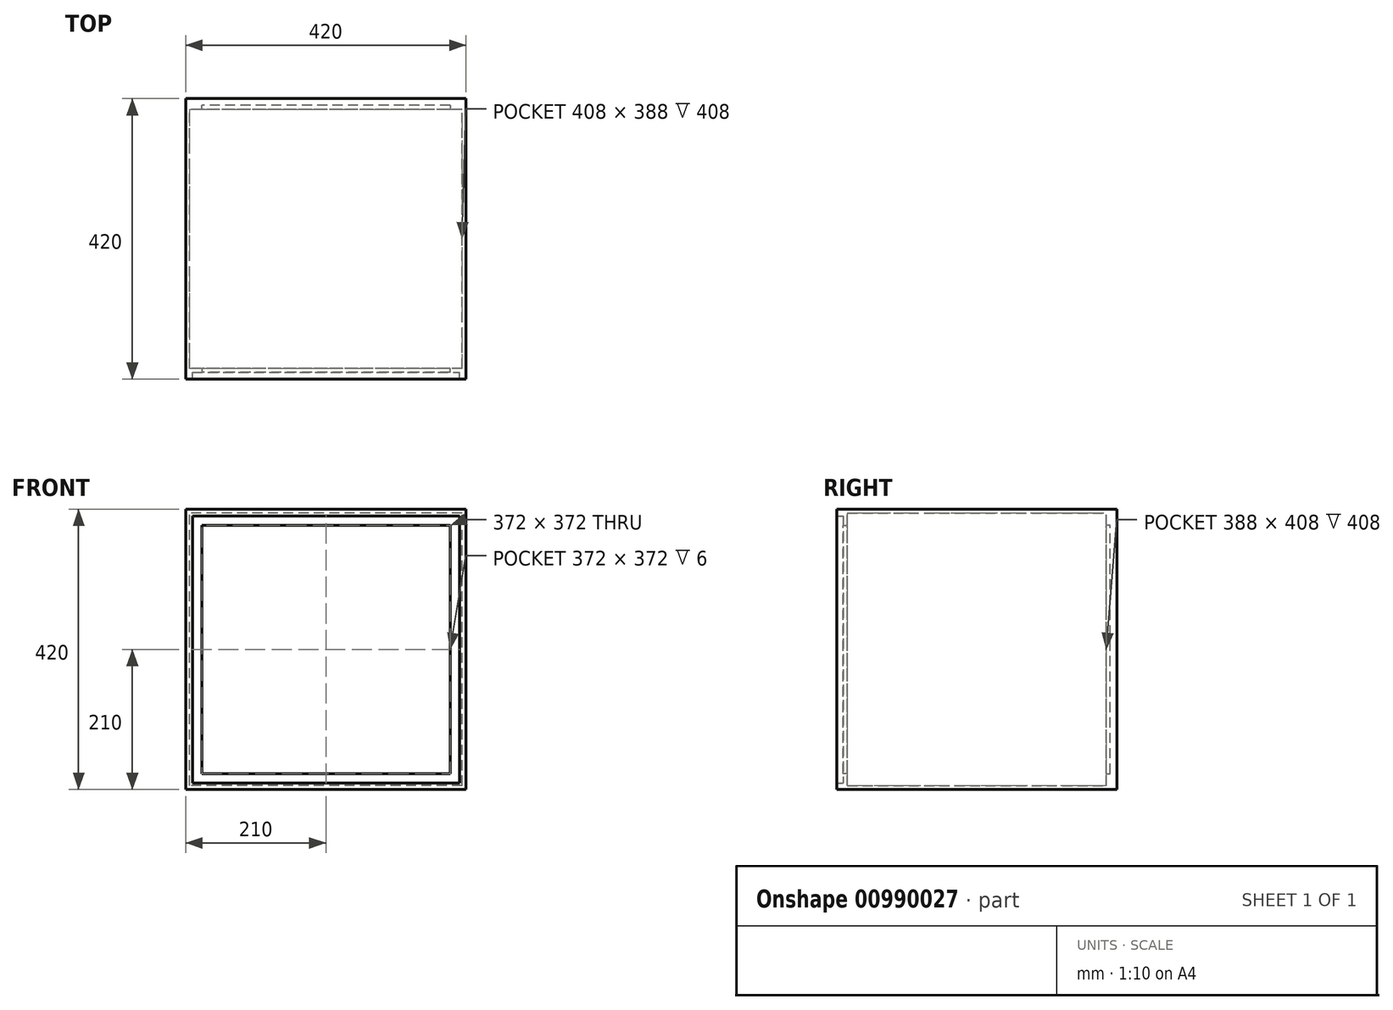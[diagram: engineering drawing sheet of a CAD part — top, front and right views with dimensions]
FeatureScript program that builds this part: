
annotation { "Feature Type Name" : "Feature", "Feature Type Description" : "" }
export const myFeature = defineFeature(function(context is Context, id is Id, definition is map)
    precondition{}
    {
        {
            var Q0;
            Q0=qCreatedBy(makeId("Front.planeOp"),FACE);
            var sketch = newSketch(context, id + "F0", { "sketchPlane" : qUnion([Q0])});
            skLineSegment(sketch, "E0.bottom", {"start": v(-210, 210) * mm, "end": v(210, 210) * mm});
            skLineSegment(sketch, "E0.top", {"start": v(-210, -210) * mm, "end": v(210, -210) * mm});
            skLineSegment(sketch, "E0.left", {"start": v(-210, 210) * mm, "end": v(-210, -210) * mm});
            skLineSegment(sketch, "E0.right", {"start": v(210, 210) * mm, "end": v(210, -210) * mm});
            skPoint(sketch, "E0.middle", {"position": v(0, 0) * mm});
            skSolve(sketch);
        }
        {
            var Q0;
            Q0=qSketchRegion(id+"F0",true);
            extrude(context, id + "F1", {"entities" : qUnion([Q0]), "endBound" : BoundingType.SYMMETRIC, "depth" : 210 * mm, "offsetDistance" : 25.4 * mm});
        }
        {
            var Q0;
            Q0=makeQuery(id+"F1.opExtrude","CAP_FACE",FACE,{"disambiguationData":[OSD([sQuery(id+"F0.wireOp",EDGE,"E0.bottom"),sQuery(id+"F0.wireOp",EDGE,"E0.top"),sQuery(id+"F0.wireOp",EDGE,"E0.left"),sQuery(id+"F0.wireOp",EDGE,"E0.right")])],"isStart":false});
            shell(context, id + "F2", {"entities" : qUnion([Q0]), "thickness" : 6 * mm});
        }
        {
            var Q0;
            Q0=makeQuery(id+"F2.opShell","OFFSET_FACE",FACE,{"disambiguationData":[OSD([sQuery(id+"F0.wireOp",EDGE,"E0.left")])]});
            var sketch = newSketch(context, id + "F3", { "sketchPlane" : qUnion([Q0])});
            skLineSegment(sketch, "E1.top", {"start": v(-2, -194) * mm, "end": v(2, -194) * mm});
            skPoint(sketch, "E1.middle", {"position": v(0, 0) * mm});
            skLineSegment(sketch, "E2.bottom", {"start": v(-89, -204) * mm, "end": v(-95, -204) * mm});
            skLineSegment(sketch, "E2.top", {"start": v(-89, 204) * mm, "end": v(-95, 204) * mm});
            skLineSegment(sketch, "E2.left", {"start": v(-89, -204) * mm, "end": v(-89, 204) * mm});
            skLineSegment(sketch, "E2.right", {"start": v(-95, -204) * mm, "end": v(-95, 204) * mm});
            skPoint(sketch, "E2.middle", {"position": v(-92, 0) * mm});
            skSolve(sketch);
        }
        {
            var Q0;
            Q0=qSketchRegion(id+"F3",true);
            extrude(context, id + "F4", {"entities" : qUnion([Q0]), "operationType" : NewBodyOperationType.ADD, "depth" : 18 * mm, "offsetDistance" : 25.4 * mm});
        }
        {
            var Q0;
            Q0=makeQuery(id+"F2.opShell","OFFSET_FACE",FACE,{"disambiguationData":[OSD([sQuery(id+"F0.wireOp",EDGE,"E0.right")])]});
            var sketch = newSketch(context, id + "F5", { "sketchPlane" : qUnion([Q0])});
            skLineSegment(sketch, "E3.bottom", {"start": v(95, -204) * mm, "end": v(89, -204) * mm});
            skLineSegment(sketch, "E3.top", {"start": v(95, 204) * mm, "end": v(89, 204) * mm});
            skLineSegment(sketch, "E3.left", {"start": v(89, -204) * mm, "end": v(89, 204) * mm});
            skLineSegment(sketch, "E3.right", {"start": v(95, -204) * mm, "end": v(95, 204) * mm});
            skPoint(sketch, "E3.middle", {"position": v(92, 0) * mm});
            skSolve(sketch);
        }
        {
            var Q0;
            Q0=qSketchRegion(id+"F5",true);
            extrude(context, id + "F6", {"entities" : qUnion([Q0]), "operationType" : NewBodyOperationType.ADD, "depth" : 18 * mm, "offsetDistance" : 25.4 * mm});
        }
        {
            var Q0;
            Q0=makeQuery(id+"F4.opExtrude","CAP_FACE",FACE,{"disambiguationData":[OSD([sQuery(id+"F3.wireOp",EDGE,"E2.bottom"),sQuery(id+"F3.wireOp",EDGE,"E2.top"),sQuery(id+"F3.wireOp",EDGE,"E2.left"),sQuery(id+"F3.wireOp",EDGE,"E2.right")])],"isStart":false});
            var sketch = newSketch(context, id + "F7", { "sketchPlane" : qUnion([Q0])});
            skLineSegment(sketch, "E4.bottom", {"start": v(-95, 204) * mm, "end": v(-89, 204) * mm});
            skLineSegment(sketch, "E4.top", {"start": v(-95, 186) * mm, "end": v(-89, 186) * mm});
            skLineSegment(sketch, "E4.left", {"start": v(-95, 204) * mm, "end": v(-95, 186) * mm});
            skLineSegment(sketch, "E4.right", {"start": v(-89, 204) * mm, "end": v(-89, 186) * mm});
            skSolve(sketch);
        }
        {
            var Q0;
            Q0=qSketchRegion(id+"F7",true);
            var Q1;
            Q1=makeQuery(id+"F6.opExtrude","CAP_FACE",FACE,{"disambiguationData":[OSD([sQuery(id+"F5.wireOp",EDGE,"E3.bottom"),sQuery(id+"F5.wireOp",EDGE,"E3.top"),sQuery(id+"F5.wireOp",EDGE,"E3.left"),sQuery(id+"F5.wireOp",EDGE,"E3.right")])],"isStart":false});
            extrude(context, id + "F8", {"entities" : qUnion([Q0]), "operationType" : NewBodyOperationType.ADD, "endBound" : BoundingType.UP_TO_SURFACE, "depth" : 12.2 * mm, "endBoundEntityFace" : qUnion([Q1]), "offsetDistance" : 25.4 * mm});
        }
        {
            var Q0;
            Q0=makeQuery(id+"F4.opExtrude","CAP_FACE",FACE,{"disambiguationData":[OSD([sQuery(id+"F3.wireOp",EDGE,"E2.bottom"),sQuery(id+"F3.wireOp",EDGE,"E2.top"),sQuery(id+"F3.wireOp",EDGE,"E2.left"),sQuery(id+"F3.wireOp",EDGE,"E2.right")])],"isStart":false});
            var sketch = newSketch(context, id + "F9", { "sketchPlane" : qUnion([Q0])});
            skLineSegment(sketch, "E5.bottom", {"start": v(-89, -204) * mm, "end": v(-95, -204) * mm});
            skLineSegment(sketch, "E5.top", {"start": v(-89, -186) * mm, "end": v(-95, -186) * mm});
            skLineSegment(sketch, "E5.left", {"start": v(-89, -204) * mm, "end": v(-89, -186) * mm});
            skLineSegment(sketch, "E5.right", {"start": v(-95, -204) * mm, "end": v(-95, -186) * mm});
            skSolve(sketch);
        }
        {
            var Q0;
            Q0=qSketchRegion(id+"F9",true);
            var Q1;
            Q1=makeQuery(id+"F6.opExtrude","CAP_FACE",FACE,{"disambiguationData":[OSD([sQuery(id+"F5.wireOp",EDGE,"E3.bottom"),sQuery(id+"F5.wireOp",EDGE,"E3.top"),sQuery(id+"F5.wireOp",EDGE,"E3.left"),sQuery(id+"F5.wireOp",EDGE,"E3.right")])],"isStart":false});
            extrude(context, id + "F10", {"entities" : qUnion([Q0]), "operationType" : NewBodyOperationType.ADD, "endBound" : BoundingType.UP_TO_SURFACE, "depth" : 25.4 * mm, "endBoundEntityFace" : qUnion([Q1]), "offsetDistance" : 25.4 * mm});
        }
        {
            var Q0;
            Q0=makeQuery(id+"F10.boolean.opBoolean","MERGE",FACE,{"derivedFrom":[makeQuery(id+"F8.boolean.opBoolean","MERGE",FACE,{"derivedFrom":[makeQuery(id+"F4.opExtrude","SWEPT_FACE",FACE,{"disambiguationData":[OSD([sQuery(id+"F3.wireOp",EDGE,"E2.right")])]}),makeQuery(id+"F6.opExtrude","SWEPT_FACE",FACE,{"disambiguationData":[OSD([sQuery(id+"F5.wireOp",EDGE,"E3.right")])]}),makeQuery(id+"F8.opExtrude","SWEPT_FACE",FACE,{"disambiguationData":[OSD([sQuery(id+"F7.wireOp",EDGE,"E4.left")])]})]}),makeQuery(id+"F10.opExtrude","SWEPT_FACE",FACE,{"disambiguationData":[OSD([sQuery(id+"F9.wireOp",EDGE,"E5.right")])]})]});
            var sketch = newSketch(context, id + "F11", { "sketchPlane" : qUnion([Q0])});
            skLineSegment(sketch, "E6.bottom", {"start": v(-204, 204) * mm, "end": v(204, 204) * mm});
            skLineSegment(sketch, "E6.top", {"start": v(-204, -204) * mm, "end": v(204, -204) * mm});
            skLineSegment(sketch, "E6.left", {"start": v(-204, 204) * mm, "end": v(-204, -204) * mm});
            skLineSegment(sketch, "E6.right", {"start": v(204, 204) * mm, "end": v(204, -204) * mm});
            skPoint(sketch, "E6.middle", {"position": v(0, 0) * mm});
            skLineSegment(sketch, "E7.bottom", {"start": v(-200, 200) * mm, "end": v(200, 200) * mm});
            skLineSegment(sketch, "E7.top", {"start": v(-200, -200) * mm, "end": v(200, -200) * mm});
            skLineSegment(sketch, "E7.left", {"start": v(-200, 200) * mm, "end": v(-200, -200) * mm});
            skLineSegment(sketch, "E7.right", {"start": v(200, 200) * mm, "end": v(200, -200) * mm});
            skSolve(sketch);
        }
        {
            var Q0;
            Q0=qSketchRegion(id+"F11",true);
            extrude(context, id + "F12", {"entities" : qUnion([Q0]), "operationType" : NewBodyOperationType.ADD, "depth" : 10 * mm, "offsetDistance" : 25.4 * mm});
        }
        {
            var Q0;
            Q0=makeQuery(id+"F1.opExtrude","SWEPT_BODY",BODY,{"disambiguationData":[OSD([sQuery(id+"F0.wireOp",EDGE,"E0.bottom"),sQuery(id+"F0.wireOp",EDGE,"E0.top"),sQuery(id+"F0.wireOp",EDGE,"E0.left"),sQuery(id+"F0.wireOp",EDGE,"E0.right")])]});
            var Q1;
            Q1=makeQuery(id+"F1.opExtrude","CAP_FACE",FACE,{"disambiguationData":[OSD([sQuery(id+"F0.wireOp",EDGE,"E0.bottom"),sQuery(id+"F0.wireOp",EDGE,"E0.top"),sQuery(id+"F0.wireOp",EDGE,"E0.left"),sQuery(id+"F0.wireOp",EDGE,"E0.right")])],"isStart":true});
            mirror(context, id + "F13", {"operationType" : NewBodyOperationType.ADD, "entities" : qUnion([Q0]), "mirrorPlane" : qUnion([Q1])});
        }
        {
            var Q0;
            Q0=makeQuery(id+"F13.opPattern","COPY",FACE,{"derivedFrom":makeQuery(id+"F2.opShell","OFFSET_FACE",FACE,{"disambiguationData":[OSD([sQuery(id+"F0.wireOp",EDGE,"E0.bottom"),sQuery(id+"F0.wireOp",EDGE,"E0.top"),sQuery(id+"F0.wireOp",EDGE,"E0.left"),sQuery(id+"F0.wireOp",EDGE,"E0.right")])]}),"instanceName":"1"});
            extrude(context, id + "F14", {"entities" : qUnion([Q0]), "operationType" : NewBodyOperationType.REMOVE, "oppositeDirection" : true, "depth" : 25.4 * mm, "offsetDistance" : 25.4 * mm});
        }
        {
            var Q0;
            Q0=makeQuery(id+"F13.opPattern","COPY",FACE,{"derivedFrom":makeQuery(id+"F10.boolean.opBoolean","MERGE",FACE,{"derivedFrom":[makeQuery(id+"F8.boolean.opBoolean","MERGE",FACE,{"derivedFrom":[makeQuery(id+"F4.opExtrude","SWEPT_FACE",FACE,{"disambiguationData":[OSD([sQuery(id+"F3.wireOp",EDGE,"E2.right")])]}),makeQuery(id+"F6.opExtrude","SWEPT_FACE",FACE,{"disambiguationData":[OSD([sQuery(id+"F5.wireOp",EDGE,"E3.right")])]}),makeQuery(id+"F8.opExtrude","SWEPT_FACE",FACE,{"disambiguationData":[OSD([sQuery(id+"F7.wireOp",EDGE,"E4.left")])]})]}),makeQuery(id+"F10.opExtrude","SWEPT_FACE",FACE,{"disambiguationData":[OSD([sQuery(id+"F9.wireOp",EDGE,"E5.right")])]})]}),"instanceName":"1"});
            var sketch = newSketch(context, id + "F15", { "sketchPlane" : qUnion([Q0])});
            skLineSegment(sketch, "E8.bottom", {"start": v(-200, 200) * mm, "end": v(200, 200) * mm});
            skLineSegment(sketch, "E8.top", {"start": v(-200, -200) * mm, "end": v(200, -200) * mm});
            skLineSegment(sketch, "E8.left", {"start": v(-200, 200) * mm, "end": v(-200, -200) * mm});
            skLineSegment(sketch, "E8.right", {"start": v(200, 200) * mm, "end": v(200, -200) * mm});
            skPoint(sketch, "E8.middle", {"position": v(0, 0) * mm});
            skSolve(sketch);
        }
        {
            var Q0;
            Q0 = qSketchRegion(id + "F15", true);
            extrude(context, id + "F16", {"entities" : qUnion([Q0]), "operationType" : NewBodyOperationType.ADD, "depth" : 10 * mm, "offsetDistance" : 25.4 * mm});
        }
    });
